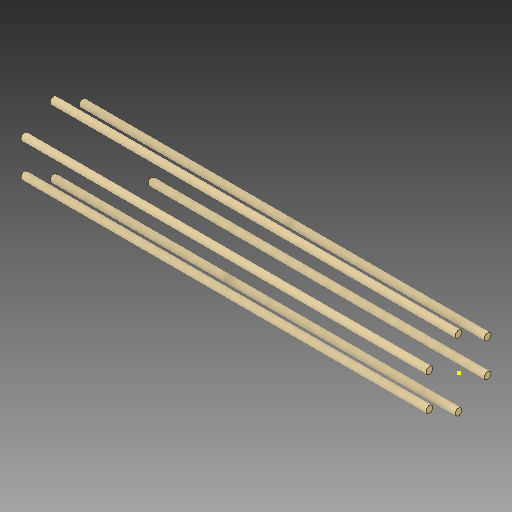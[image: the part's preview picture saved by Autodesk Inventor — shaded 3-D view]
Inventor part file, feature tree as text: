
AUTODESK INVENTOR PART (.ipt)
format: ipt  version: 2017.3 (Build 213256000, 256)  size: 133,632 bytes
history: native  units: mm
features: sketch x5, extrude x4
ambient origin geometry x8: Origin, YZ Plane, XZ Plane, XY Plane, X Axis, Y Axis, Z Axis, Center Point
bodies: Solid1 (feature_tree)
feature tree (9):
  extrude  "Extrusion1"  Depth=1.0mm TaperAngle=0.0deg
  extrude  "Extrusion2"  Depth=1.6mm
  sketch  "Sketch3"  dims[d6=1.6mm d7=1.6mm]
  extrude  "Extrusion3"  Depth=1.6mm
  extrude  "Extrusion4"  Depth=1.6mm
  sketch  "Sketch1"  dims[d0=19.0mm d1=1.0mm d2=0.0mm]
  sketch  "Sketch2"  dims[d4=1.6mm d5=1.6mm]
  sketch  "Sketch4"  dims[d8=1.6mm d9=1.6mm]
  sketch  "Sketch5"  dims[d10=99.0mm d11=0.0mm d12=6.0mm d13=0.0mm d14=16.0mm d15=0.0mm]
